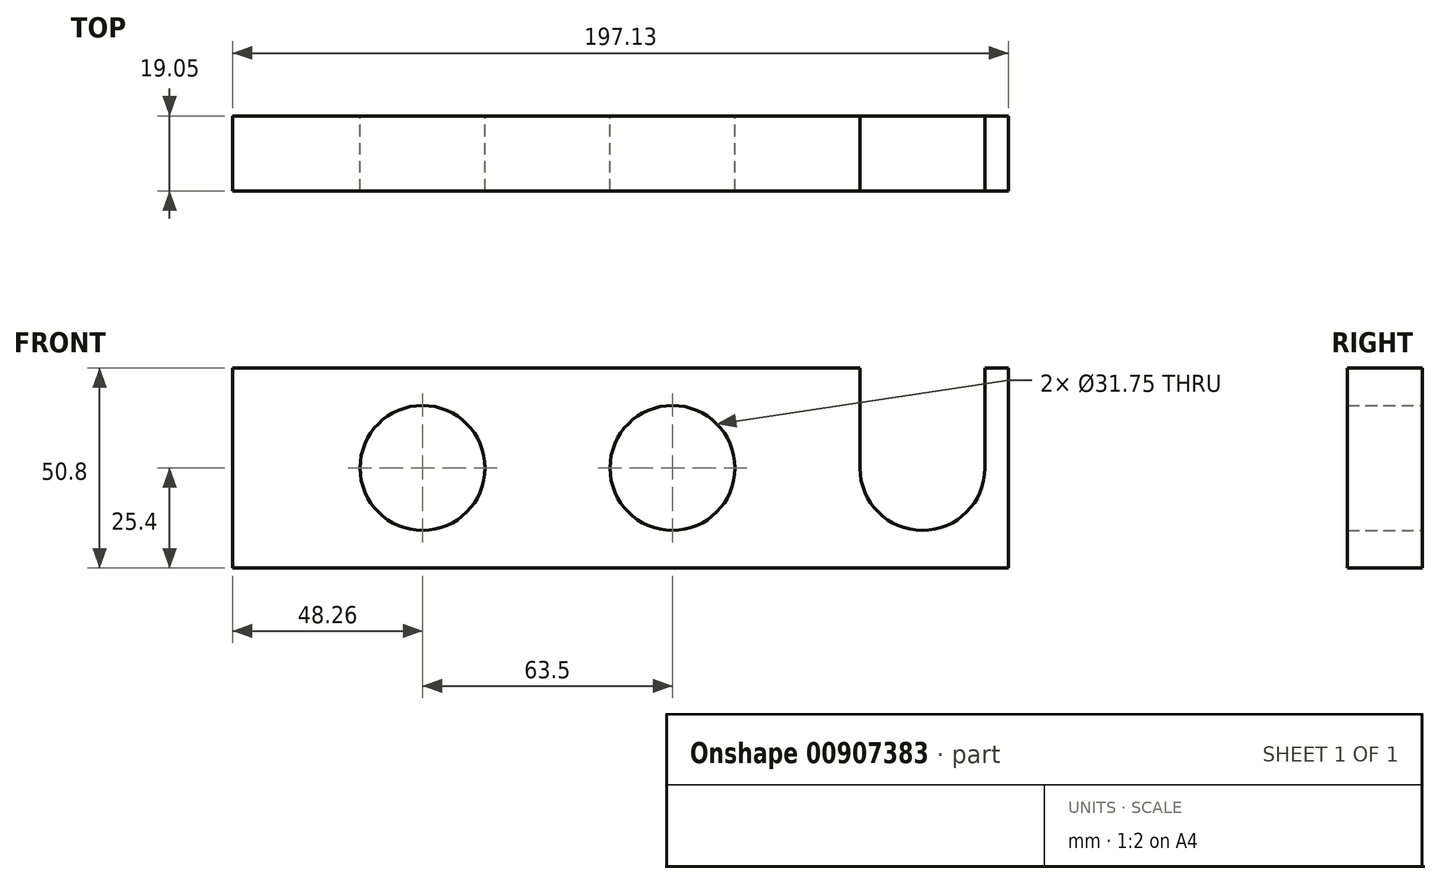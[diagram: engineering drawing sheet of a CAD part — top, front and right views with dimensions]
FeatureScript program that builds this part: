
annotation { "Feature Type Name" : "Feature", "Feature Type Description" : "" }
export const myFeature = defineFeature(function(context is Context, id is Id, definition is map)
    precondition{}
    {
        {
            var Q0;
            Q0=qCreatedBy(makeId("Front.planeOp"),FACE);
            var sketch = newSketch(context, id + "F0", { "sketchPlane" : qUnion([Q0])});
            skLineSegment(sketch, "E0.bottom", {"start": v(82.83, -25.4) * mm, "end": v(-114.3, -25.4) * mm});
            skLineSegment(sketch, "E0.top", {"start": v(82.83, 25.4) * mm, "end": v(76.83, 25.4) * mm});
            skLineSegment(sketch, "E0.right", {"start": v(-114.3, -25.4) * mm, "end": v(-114.3, 25.4) * mm});
            skPoint(sketch, "E0.middle", {"position": v(0, 0) * mm});
            skCircle(sketch, "E1", {"center": v(-66.04, 0) * mm, "radius": 15.88 * mm});
            skCircle(sketch, "E2.1.0.1", {"center": v(-2.54, 0) * mm, "radius": 15.88 * mm});
            skArc(sketch, "E2.2.0.1", {"start": v(45.08, 0) * mm, "mid": v(60.96, -15.88) * mm, "end": v(76.83, 0) * mm});
            skLineSegment(sketch, "E2.direction1", {"start": v(-114.3, 25.4) * mm, "end": v(-50.8, 25.4) * mm, "construction": true});
            skLineSegment(sketch, "E3", {"start": v(45.08, 0) * mm, "end": v(45.08, 25.4) * mm});
            skLineSegment(sketch, "E4", {"start": v(76.83, 0) * mm, "end": v(76.83, 25.4) * mm});
            skLineSegment(sketch, "E5.trimOffspring", {"start": v(45.08, 25.4) * mm, "end": v(-114.3, 25.4) * mm});
            skLineSegment(sketch, "E6", {"start": v(82.83, 25.4) * mm, "end": v(82.83, -25.4) * mm});
            skSolve(sketch);
        }
        {
            var Q0;
            Q0 = qSketchRegion(id + "F0", true);
            extrude(context, id + "F1", {"entities" : qUnion([Q0]), "depth" : 19.05 * mm, "offsetDistance" : 25.4 * mm});
        }
    });
